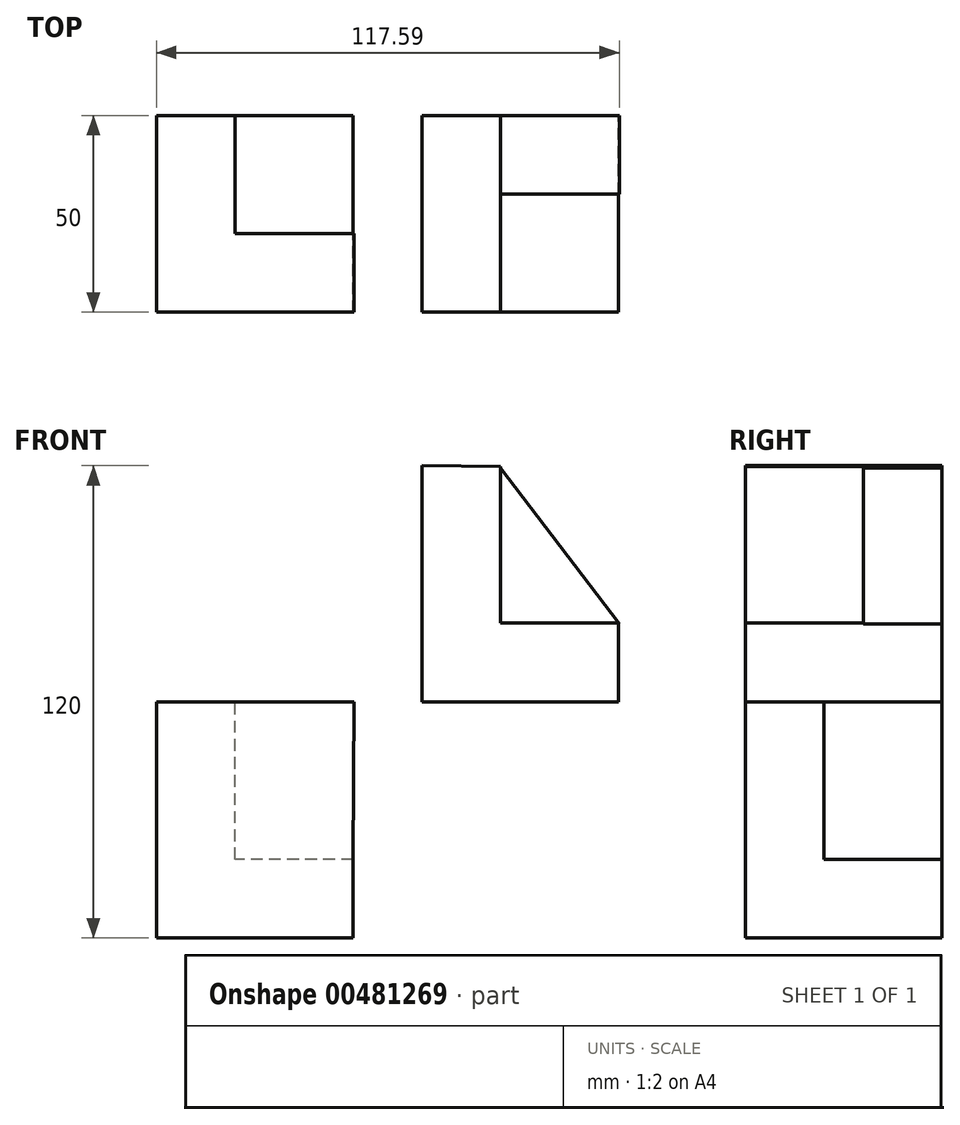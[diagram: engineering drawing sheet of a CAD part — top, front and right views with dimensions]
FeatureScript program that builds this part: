
annotation { "Feature Type Name" : "Feature", "Feature Type Description" : "" }
export const myFeature = defineFeature(function(context is Context, id is Id, definition is map)
    precondition{}
    {
        {
            var Q0;
            Q0=qCreatedBy(makeId("Front.planeOp"),FACE);
            var sketch = newSketch(context, id + "F0", { "sketchPlane" : qUnion([Q0])});
            skLineSegment(sketch, "E0", {"start": v(0, 0) * mm, "end": v(0, 60) * mm});
            skLineSegment(sketch, "E1", {"start": v(0, 60) * mm, "end": v(20, 59.78) * mm});
            skLineSegment(sketch, "E2", {"start": v(20, 59.78) * mm, "end": v(20, 20) * mm});
            skLineSegment(sketch, "E3", {"start": v(20, 20) * mm, "end": v(50, 20) * mm});
            skLineSegment(sketch, "E4", {"start": v(50, 20) * mm, "end": v(50, 0) * mm});
            skLineSegment(sketch, "E5", {"start": v(50, 0) * mm, "end": v(0, 0) * mm});
            skSolve(sketch);
        }
        {
            var Q0;
            Q0=makeQuery(id+"F0.imprint","IMPRINT",FACE,{"disambiguationData":[TD([[makeQuery(id+"F0.imprint","IMPRINT",EDGE,{"derivedFrom":sQuery(id+"F0.wireOp",EDGE,"E0")}),-1.0]])]});
            extrude(context, id + "F1", {"entities" : qUnion([Q0]), "depth" : 50 * mm});
        }
        {
            var Q0;
            Q0=makeQuery(id+"F0.imprint","IMPRINT",FACE,{"disambiguationData":[TD([[makeQuery(id+"F0.imprint","IMPRINT",EDGE,{"derivedFrom":sQuery(id+"F0.wireOp",EDGE,"E0")}),-1.0]])]});
            var sketch = newSketch(context, id + "F2", { "sketchPlane" : qUnion([Q0])});
            skLineSegment(sketch, "E6", {"start": v(19.55, 60.05) * mm, "end": v(50.14, 19.83) * mm});
            skLineSegment(sketch, "E7", {"start": v(50.14, 19.83) * mm, "end": v(19.55, 19.83) * mm});
            skLineSegment(sketch, "E8", {"start": v(19.55, 19.83) * mm, "end": v(19.55, 60.05) * mm});
            skSolve(sketch);
        }
        {
            var Q0;
            {var subQ0=makeQuery(id+"F0.imprint","IMPRINT",EDGE,{"derivedFrom":sQuery(id+"F0.wireOp",EDGE,"E3")});Q0=makeQuery(id+"F2.imprint","IMPRINT",FACE,{"disambiguationData":[TD([[makeQuery(id+"F2.imprint","IMPRINT",EDGE,{"derivedFrom":subQ0}),1.0]])]});}
            extrude(context, id + "F3", {"entities" : qUnion([Q0]), "operationType" : NewBodyOperationType.ADD, "depth" : 20 * mm});
        }
        {
            var Q0;
            Q0=qCreatedBy(makeId("Front.planeOp"),FACE);
            var sketch = newSketch(context, id + "F4", { "sketchPlane" : qUnion([Q0])});
            skLineSegment(sketch, "E9", {"start": v(-67.45, 0) * mm, "end": v(-67.45, -60) * mm});
            skLineSegment(sketch, "E10", {"start": v(-67.45, -60) * mm, "end": v(-17.45, -60) * mm});
            skLineSegment(sketch, "E11", {"start": v(-17.45, -60) * mm, "end": v(-17.45, -40) * mm});
            skLineSegment(sketch, "E12", {"start": v(-17.45, -40) * mm, "end": v(-47.45, -40) * mm});
            skLineSegment(sketch, "E13", {"start": v(-47.45, -40) * mm, "end": v(-47.45, 0) * mm});
            skLineSegment(sketch, "E14", {"start": v(-47.45, 0) * mm, "end": v(-67.45, 0) * mm});
            skSolve(sketch);
        }
        {
            var Q0;
            Q0=makeQuery(id+"F4.imprint","IMPRINT",FACE,{"disambiguationData":[TD([[makeQuery(id+"F4.imprint","IMPRINT",EDGE,{"derivedFrom":sQuery(id+"F4.wireOp",EDGE,"E9")}),1.0]])]});
            extrude(context, id + "F5", {"entities" : qUnion([Q0]), "depth" : 50 * mm});
        }
        {
            var Q0;
            Q0=makeQuery(id+"F5.opExtrude","CAP_FACE",FACE,{"disambiguationData":[OSD([sQuery(id+"F4.wireOp",EDGE,"E9"),sQuery(id+"F4.wireOp",EDGE,"E10"),sQuery(id+"F4.wireOp",EDGE,"E11"),sQuery(id+"F4.wireOp",EDGE,"E12"),sQuery(id+"F4.wireOp",EDGE,"E13"),sQuery(id+"F4.wireOp",EDGE,"E14")])],"isStart":false});
            var sketch = newSketch(context, id + "F6", { "sketchPlane" : qUnion([Q0])});
            skLineSegment(sketch, "E15", {"start": v(-47.45, 0) * mm, "end": v(-17.28, 0) * mm});
            skLineSegment(sketch, "E16", {"start": v(-17.28, 0) * mm, "end": v(-17.45, -40) * mm});
            skLineSegment(sketch, "E17", {"start": v(-17.45, -40) * mm, "end": v(-47.45, -40) * mm});
            skLineSegment(sketch, "E18", {"start": v(-47.45, -40) * mm, "end": v(-47.45, 0) * mm});
            skSolve(sketch);
        }
        {
            var Q0;
            Q0=makeQuery(id+"F6.imprint","IMPRINT",FACE,{"disambiguationData":[TD([[makeQuery(id+"F6.imprint","IMPRINT",EDGE,{"derivedFrom":sQuery(id+"F6.wireOp",EDGE,"E15")}),-1.0]])]});
            extrude(context, id + "F7", {"entities" : qUnion([Q0]), "operationType" : NewBodyOperationType.ADD, "oppositeDirection" : true, "depth" : 20 * mm});
        }
    });
